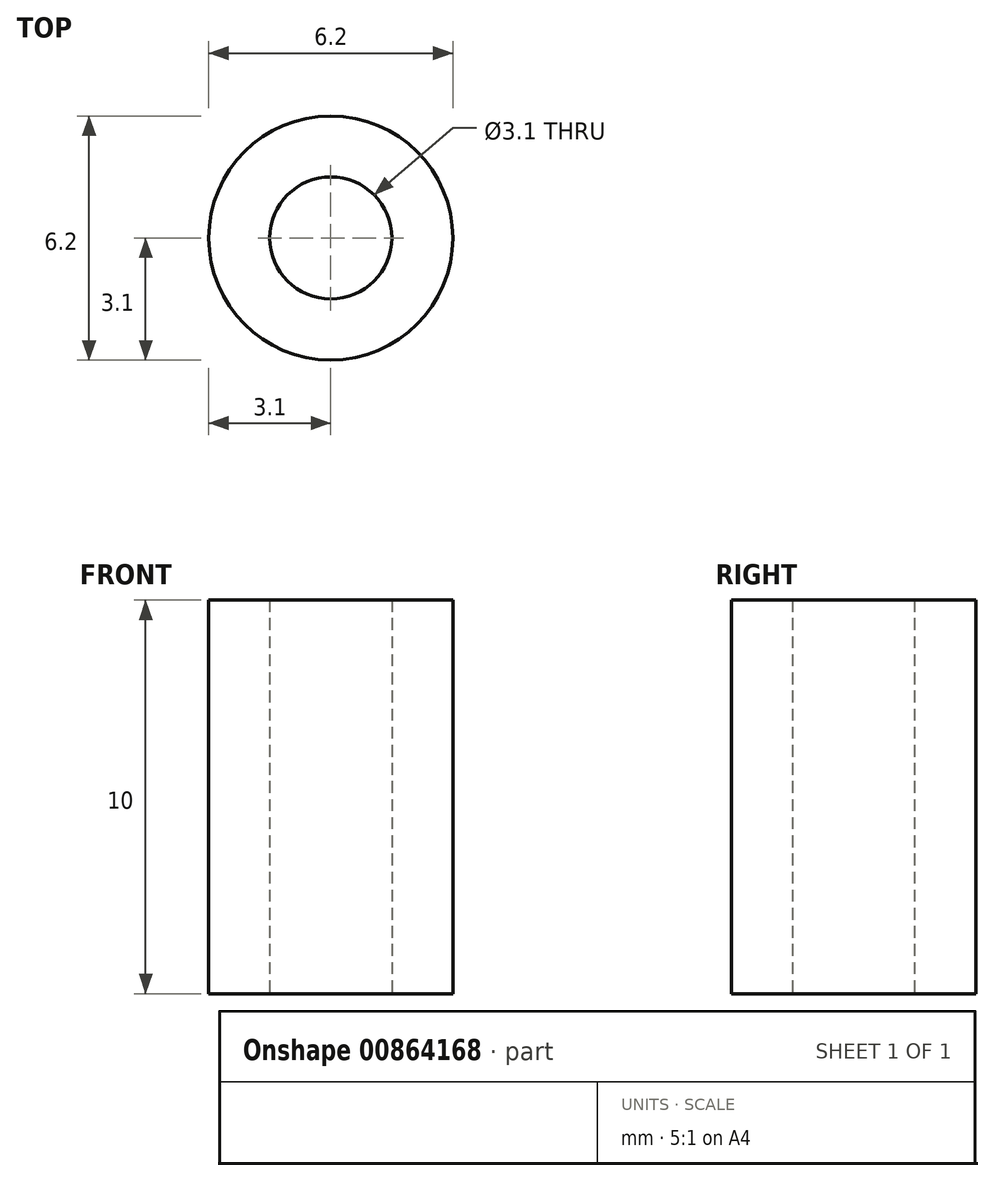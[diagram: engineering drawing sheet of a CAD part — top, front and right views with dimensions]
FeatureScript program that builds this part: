
annotation { "Feature Type Name" : "Feature", "Feature Type Description" : "" }
export const myFeature = defineFeature(function(context is Context, id is Id, definition is map)
    precondition{}
    {
        {
            var Q0;
            Q0=qCreatedBy(makeId("Top.planeOp"),FACE);
            var sketch = newSketch(context, id + "F0", { "sketchPlane" : qUnion([Q0])});
            skCircle(sketch, "E0", {"center": v(0, 0) * mm, "radius": 3.1 * mm});
            skCircle(sketch, "E1", {"center": v(0, 0) * mm, "radius": 1.55 * mm});
            skSolve(sketch);
        }
        {
            var Q0;
            Q0 = qSketchRegion(id + "F0", true);
            extrude(context, id + "F1", {"entities" : qUnion([Q0]), "depth" : 10 * mm, "offsetDistance" : 25 * mm});
        }
    });
